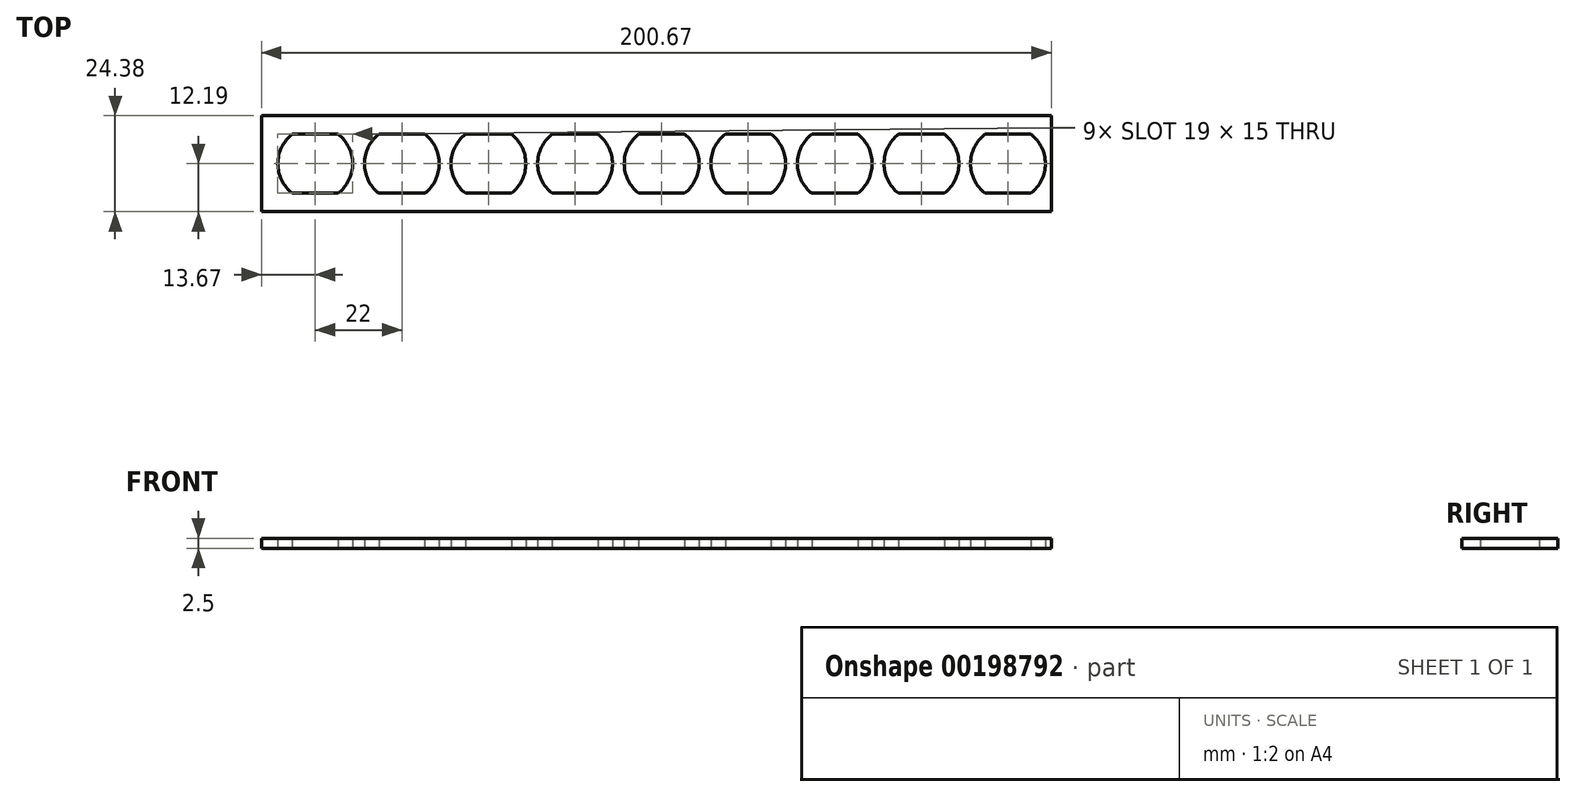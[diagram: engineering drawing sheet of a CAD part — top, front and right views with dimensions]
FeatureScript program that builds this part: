
annotation { "Feature Type Name" : "Feature", "Feature Type Description" : "" }
export const myFeature = defineFeature(function(context is Context, id is Id, definition is map)
    precondition{}
    {
        {
            var Q0;
            Q0=qCreatedBy(makeId("Top.planeOp"),FACE);
            var sketch = newSketch(context, id + "F0", { "sketchPlane" : qUnion([Q0])});
            skArc(sketch, "E0", {"start": v(-5.83, 7.5) * mm, "mid": v(-9.5, 0) * mm, "end": v(-5.83, -7.5) * mm});
            skLineSegment(sketch, "E1.bottom", {"start": v(-5.83, 7.5) * mm, "end": v(5.83, 7.5) * mm});
            skLineSegment(sketch, "E1.top", {"start": v(-5.83, -7.5) * mm, "end": v(5.83, -7.5) * mm});
            skLineSegment(sketch, "E2", {"start": v(-5.83, 7.5) * mm, "end": v(-5.83, -7.5) * mm, "construction": true});
            skLineSegment(sketch, "E3", {"start": v(5.83, 7.5) * mm, "end": v(5.83, -7.5) * mm, "construction": true});
            skArc(sketch, "E4.trimOffspring", {"start": v(5.83, -7.5) * mm, "mid": v(9.5, 0) * mm, "end": v(5.83, 7.5) * mm});
            skArc(sketch, "E5.1.0.0", {"start": v(16.17, 7.5) * mm, "mid": v(12.5, 0) * mm, "end": v(16.17, -7.5) * mm});
            skLineSegment(sketch, "E5.1.0.1", {"start": v(16.17, 7.5) * mm, "end": v(27.83, 7.5) * mm});
            skArc(sketch, "E5.1.0.2", {"start": v(27.83, -7.5) * mm, "mid": v(31.5, 0) * mm, "end": v(27.83, 7.5) * mm});
            skLineSegment(sketch, "E5.1.0.3", {"start": v(16.17, -7.5) * mm, "end": v(27.83, -7.5) * mm});
            skArc(sketch, "E5.2.0.0", {"start": v(38.17, 7.5) * mm, "mid": v(34.5, 0) * mm, "end": v(38.17, -7.5) * mm});
            skLineSegment(sketch, "E5.2.0.1", {"start": v(38.17, 7.5) * mm, "end": v(49.83, 7.5) * mm});
            skArc(sketch, "E5.2.0.2", {"start": v(49.83, -7.5) * mm, "mid": v(53.5, 0) * mm, "end": v(49.83, 7.5) * mm});
            skLineSegment(sketch, "E5.2.0.3", {"start": v(38.17, -7.5) * mm, "end": v(49.83, -7.5) * mm});
            skArc(sketch, "E5.3.0.0", {"start": v(60.17, 7.5) * mm, "mid": v(56.5, 0) * mm, "end": v(60.17, -7.5) * mm});
            skLineSegment(sketch, "E5.3.0.1", {"start": v(60.17, 7.5) * mm, "end": v(71.83, 7.5) * mm});
            skArc(sketch, "E5.3.0.2", {"start": v(71.83, -7.5) * mm, "mid": v(75.5, 0) * mm, "end": v(71.83, 7.5) * mm});
            skLineSegment(sketch, "E5.3.0.3", {"start": v(60.17, -7.5) * mm, "end": v(71.83, -7.5) * mm});
            skArc(sketch, "E5.4.0.0", {"start": v(82.17, 7.5) * mm, "mid": v(78.5, 0) * mm, "end": v(82.17, -7.5) * mm});
            skLineSegment(sketch, "E5.4.0.1", {"start": v(82.17, 7.5) * mm, "end": v(93.83, 7.5) * mm});
            skArc(sketch, "E5.4.0.2", {"start": v(93.83, -7.5) * mm, "mid": v(97.5, 0) * mm, "end": v(93.83, 7.5) * mm});
            skLineSegment(sketch, "E5.4.0.3", {"start": v(82.17, -7.5) * mm, "end": v(93.83, -7.5) * mm});
            skArc(sketch, "E5.5.0.0", {"start": v(104.17, 7.5) * mm, "mid": v(100.5, 0) * mm, "end": v(104.17, -7.5) * mm});
            skLineSegment(sketch, "E5.5.0.1", {"start": v(104.17, 7.5) * mm, "end": v(115.83, 7.5) * mm});
            skArc(sketch, "E5.5.0.2", {"start": v(115.83, -7.5) * mm, "mid": v(119.5, 0) * mm, "end": v(115.83, 7.5) * mm});
            skLineSegment(sketch, "E5.5.0.3", {"start": v(104.17, -7.5) * mm, "end": v(115.83, -7.5) * mm});
            skArc(sketch, "E5.6.0.0", {"start": v(126.17, 7.5) * mm, "mid": v(122.5, 0) * mm, "end": v(126.17, -7.5) * mm});
            skLineSegment(sketch, "E5.6.0.1", {"start": v(126.17, 7.5) * mm, "end": v(137.83, 7.5) * mm});
            skArc(sketch, "E5.6.0.2", {"start": v(137.83, -7.5) * mm, "mid": v(141.5, 0) * mm, "end": v(137.83, 7.5) * mm});
            skLineSegment(sketch, "E5.6.0.3", {"start": v(126.17, -7.5) * mm, "end": v(137.83, -7.5) * mm});
            skArc(sketch, "E5.7.0.0", {"start": v(148.17, 7.5) * mm, "mid": v(144.5, 0) * mm, "end": v(148.17, -7.5) * mm});
            skLineSegment(sketch, "E5.7.0.1", {"start": v(148.17, 7.5) * mm, "end": v(159.83, 7.5) * mm});
            skArc(sketch, "E5.7.0.2", {"start": v(159.83, -7.5) * mm, "mid": v(163.5, 0) * mm, "end": v(159.83, 7.5) * mm});
            skLineSegment(sketch, "E5.7.0.3", {"start": v(148.17, -7.5) * mm, "end": v(159.83, -7.5) * mm});
            skArc(sketch, "E5.8.0.0", {"start": v(170.17, 7.5) * mm, "mid": v(166.5, 0) * mm, "end": v(170.17, -7.5) * mm});
            skLineSegment(sketch, "E5.8.0.1", {"start": v(170.17, 7.5) * mm, "end": v(181.83, 7.5) * mm});
            skArc(sketch, "E5.8.0.2", {"start": v(181.83, -7.5) * mm, "mid": v(185.5, 0) * mm, "end": v(181.83, 7.5) * mm});
            skLineSegment(sketch, "E5.8.0.3", {"start": v(170.17, -7.5) * mm, "end": v(181.83, -7.5) * mm});
            skLineSegment(sketch, "E5.direction1", {"start": v(-5.83, -7.5) * mm, "end": v(16.17, -7.5) * mm, "construction": true});
            skLineSegment(sketch, "E6.bottom", {"start": v(-13.67, 12.2) * mm, "end": v(187, 12.2) * mm});
            skLineSegment(sketch, "E6.top", {"start": v(-13.67, -12.2) * mm, "end": v(187, -12.2) * mm});
            skLineSegment(sketch, "E6.left", {"start": v(-13.67, 12.2) * mm, "end": v(-13.67, -12.2) * mm});
            skLineSegment(sketch, "E6.right", {"start": v(187, 12.2) * mm, "end": v(187, -12.2) * mm});
            skLineSegment(sketch, "E7", {"start": v(0, 0) * mm, "end": v(22, 0) * mm, "construction": true});
            skLineSegment(sketch, "E8", {"start": v(11, 0) * mm, "end": v(11, 12.2) * mm, "construction": true});
            skSolve(sketch);
        }
        {
            var Q0;
            Q0=qSketchRegion(id+"F0",true);
            extrude(context, id + "F1", {"entities" : qUnion([Q0]), "depth" : 2.5 * mm});
        }
    });
